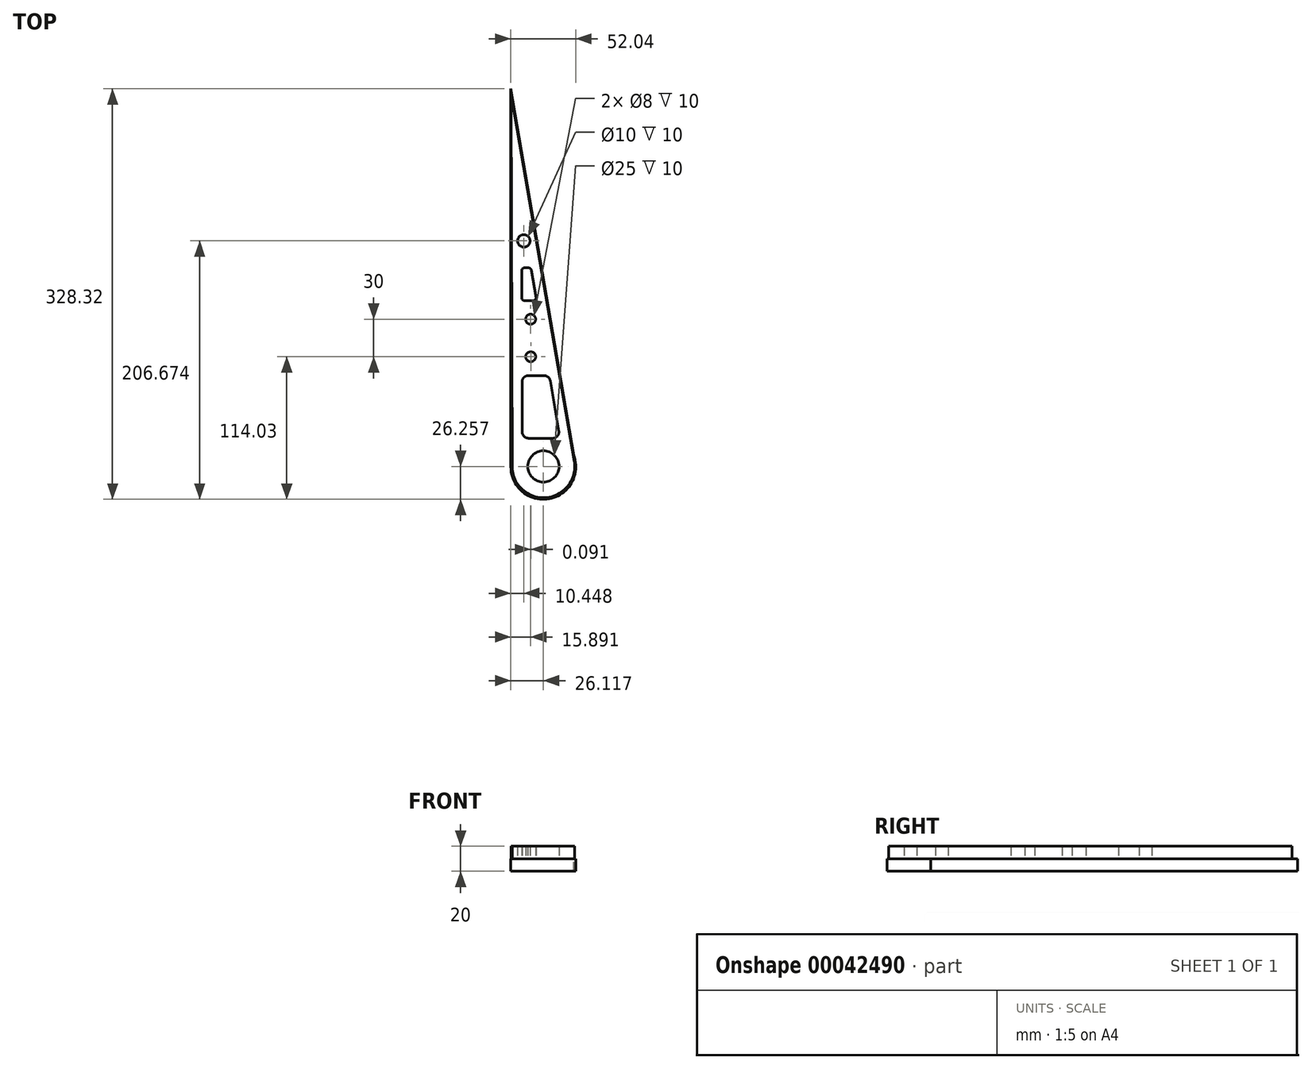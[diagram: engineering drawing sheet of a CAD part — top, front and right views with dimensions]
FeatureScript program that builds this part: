
annotation { "Feature Type Name" : "Feature", "Feature Type Description" : "" }
export const myFeature = defineFeature(function(context is Context, id is Id, definition is map)
    precondition{}
    {
        {
            var Q0;
            Q0=qCreatedBy(makeId("Top.planeOp"),FACE);
            var sketch = newSketch(context, id + "F0", { "sketchPlane" : qUnion([Q0])});
            skLineSegment(sketch, "E0", {"start": v(-19.63, -57.7) * mm, "end": v(-20.54, 242.3) * mm});
            skArc(sketch, "E1", {"start": v(-19.63, -57.7) * mm, "mid": v(8.6, -79.95) * mm, "end": v(29.85, -50.96) * mm});
            skPoint(sketch, "E1.second.point", {"position": v(-6.38, -77.32) * mm});
            skPoint(sketch, "E1.third.point", {"position": v(23.08, -37.7) * mm});
            skLineSegment(sketch, "E2", {"start": v(-20.54, 242.3) * mm, "end": v(29.85, -50.96) * mm});
            skCircle(sketch, "E3", {"center": v(5.23, -55.2) * mm, "radius": 12.5 * mm});
            skLineSegment(sketch, "E4", {"start": v(-10.05, 77.5) * mm, "end": v(-2.71, 77.5) * mm});
            skPoint(sketch, "E5.start.orphan", {"position": v(-20.09, 92.3) * mm});
            skCircle(sketch, "E6", {"center": v(-10.44, 125.22) * mm, "radius": 5 * mm});
            skLineSegment(sketch, "E7", {"start": v(-10.12, 103.63) * mm, "end": v(-6.52, 103.63) * mm});
            skLineSegment(sketch, "E8", {"start": v(-12.12, 101.62) * mm, "end": v(-12.05, 79.5) * mm});
            skLineSegment(sketch, "E9", {"start": v(-6.73, -32.62) * mm, "end": v(12.65, -32.62) * mm});
            skPoint(sketch, "E10.orphan", {"position": v(20.45, -43.47) * mm});
            skLineSegment(sketch, "E11.trimOffspring", {"start": v(10.68, 13.35) * mm, "end": v(17.58, -26.77) * mm});
            skPoint(sketch, "E12.orphan", {"position": v(4.75, 47.86) * mm});
            skLineSegment(sketch, "E13.trimOffspring", {"start": v(-11.85, 12.48) * mm, "end": v(-11.73, -27.63) * mm});
            skLineSegment(sketch, "E14.trimOffspring", {"start": v(-6.85, 17.5) * mm, "end": v(5.76, 17.5) * mm});
            skLineSegment(sketch, "E15.trimOffspring", {"start": v(-4.54, 101.96) * mm, "end": v(-0.74, 79.84) * mm});
            skPoint(sketch, "E16.orphan", {"position": v(-10.94, 139.18) * mm});
            skPoint(sketch, "E17.visualSharp", {"position": v(-11.71, -32.62) * mm});
            skArc(sketch, "E17.filletArc", {"start": v(-11.73, -27.63) * mm, "mid": v(-10.26, -31.16) * mm, "end": v(-6.73, -32.62) * mm});
            skPoint(sketch, "E18.visualSharp", {"position": v(18.58, -32.62) * mm});
            skArc(sketch, "E18.filletArc", {"start": v(12.65, -32.62) * mm, "mid": v(16.47, -30.84) * mm, "end": v(17.58, -26.77) * mm});
            skPoint(sketch, "E19.visualSharp", {"position": v(-11.86, 17.5) * mm});
            skArc(sketch, "E19.filletArc", {"start": v(-6.85, 17.5) * mm, "mid": v(-10.39, 16.03) * mm, "end": v(-11.85, 12.48) * mm});
            skPoint(sketch, "E20.visualSharp", {"position": v(9.97, 17.5) * mm});
            skArc(sketch, "E20.filletArc", {"start": v(10.68, 13.35) * mm, "mid": v(8.98, 16.32) * mm, "end": v(5.76, 17.5) * mm});
            skPoint(sketch, "E21.visualSharp", {"position": v(-4.83, 103.63) * mm});
            skArc(sketch, "E21.filletArc", {"start": v(-4.54, 101.96) * mm, "mid": v(-5.23, 103.15) * mm, "end": v(-6.52, 103.63) * mm});
            skPoint(sketch, "E22.visualSharp", {"position": v(-12.12, 103.63) * mm});
            skArc(sketch, "E22.filletArc", {"start": v(-10.12, 103.63) * mm, "mid": v(-11.53, 103.04) * mm, "end": v(-12.12, 101.62) * mm});
            skPoint(sketch, "E23.visualSharp", {"position": v(-12.04, 77.5) * mm});
            skArc(sketch, "E23.filletArc", {"start": v(-12.05, 79.5) * mm, "mid": v(-11.46, 78.08) * mm, "end": v(-10.05, 77.5) * mm});
            skPoint(sketch, "E24.visualSharp", {"position": v(-0.34, 77.5) * mm});
            skArc(sketch, "E24.filletArc", {"start": v(-2.71, 77.5) * mm, "mid": v(-1.18, 78.21) * mm, "end": v(-0.74, 79.84) * mm});
            skLineSegment(sketch, "E25", {"start": v(-5.04, 75.08) * mm, "end": v(-4.88, 22.28) * mm, "construction": true});
            skCircle(sketch, "E26", {"center": v(-5, 62.58) * mm, "radius": 4 * mm});
            skCircle(sketch, "E27", {"center": v(-4.9, 32.58) * mm, "radius": 4 * mm});
            skSolve(sketch);
        }
        {
            var Q0;
            Q0=qSketchRegion(id+"F0",true);
            extrude(context, id + "F1", {"entities" : qUnion([Q0]), "endBound" : BoundingType.SYMMETRIC, "depth" : 20 * mm});
        }
        {
            var Q0;
            Q0=qCreatedBy(makeId("Top.planeOp"),FACE);
            var sketch = newSketch(context, id + "F2", { "sketchPlane" : qUnion([Q0])});
            skLineSegment(sketch, "E28", {"start": v(-12.33, 113.45) * mm, "end": v(-12.33, -47.83) * mm});
            skLineSegment(sketch, "E29", {"start": v(-7.25, 142.54) * mm, "end": v(23.65, -54.83) * mm});
            skLineSegment(sketch, "E30", {"start": v(-12.33, 142.54) * mm, "end": v(-7.25, 142.54) * mm});
            skArc(sketch, "E31", {"start": v(-12.33, -47.83) * mm, "mid": v(1.18, -74.37) * mm, "end": v(23.65, -54.83) * mm});
            skPoint(sketch, "E32.orphan", {"position": v(-12.33, -54.83) * mm});
            skLineSegment(sketch, "E33", {"start": v(-12.33, 113.45) * mm, "end": v(-17.76, 116.29) * mm});
            skLineSegment(sketch, "E34", {"start": v(-17.76, 116.29) * mm, "end": v(-12.33, 142.54) * mm});
            skSolve(sketch);
        }
        {
            var Q0;
            Q0=qSketchRegion(id+"F2",true);
            extrude(context, id + "F3", {"entities" : qUnion([Q0]), "operationType" : NewBodyOperationType.ADD, "oppositeDirection" : true, "depth" : 10 * mm});
        }
        {
            var Q0;
            Q0=qCreatedBy(makeId("Top.planeOp"),FACE);
            var sketch = newSketch(context, id + "F4", { "sketchPlane" : qUnion([Q0])});
            skCircle(sketch, "E35", {"center": v(5.15, -55.45) * mm, "radius": 26 * mm});
            skLineSegment(sketch, "E36", {"start": v(-20.89, 246.87) * mm, "end": v(-20.85, -55.46) * mm});
            skLineSegment(sketch, "E37", {"start": v(-20.25, 111.25) * mm, "end": v(-20.25, 103.43) * mm});
            skLineSegment(sketch, "E38", {"start": v(-20.89, 246.87) * mm, "end": v(31.14, -55.9) * mm});
            skSolve(sketch);
        }
        {
            var Q0;
            Q0=qSketchRegion(id+"F4",true);
            extrude(context, id + "F5", {"entities" : qUnion([Q0]), "operationType" : NewBodyOperationType.ADD, "oppositeDirection" : true, "depth" : 10 * mm});
        }
    });
